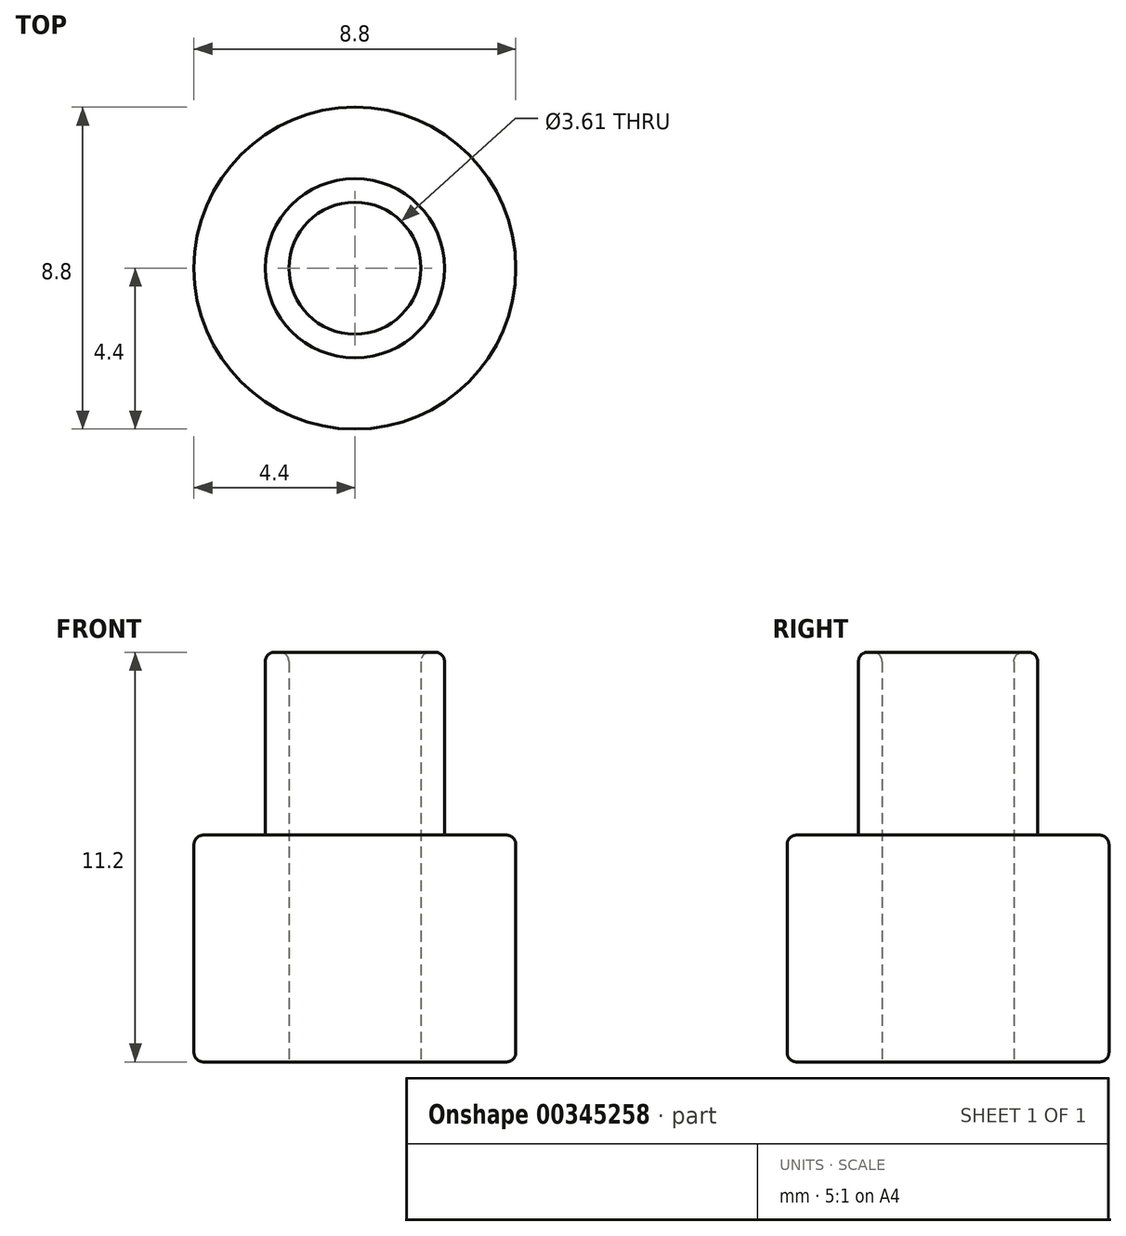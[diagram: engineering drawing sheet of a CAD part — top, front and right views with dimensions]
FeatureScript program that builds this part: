
annotation { "Feature Type Name" : "Feature", "Feature Type Description" : "" }
export const myFeature = defineFeature(function(context is Context, id is Id, definition is map)
    precondition{}
    {
        {
            var Q0;
            Q0=qCreatedBy(makeId("Top.planeOp"),FACE);
            var sketch = newSketch(context, id + "F0", { "sketchPlane" : qUnion([Q0])});
            skCircle(sketch, "E0", {"center": v(0, 0) * mm, "radius": 4.4 * mm});
            skSolve(sketch);
        }
        {
            var Q0;
            Q0 = qSketchRegion(id + "F0", true);
            extrude(context, id + "F1", {"entities" : qUnion([Q0]), "depth" : 6.2 * mm});
        }
        {
            var Q0;
            Q0=makeQuery(id+"F1.opExtrude","CAP_FACE",FACE,{"disambiguationData":[OSD([sQuery(id+"F0.wireOp",EDGE,"E0")])],"isStart":false});
            var sketch = newSketch(context, id + "F2", { "sketchPlane" : qUnion([Q0])});
            skCircle(sketch, "E1", {"center": v(0, 0) * mm, "radius": 2.45 * mm});
            skSolve(sketch);
        }
        {
            var Q0;
            Q0 = qSketchRegion(id + "F2", true);
            extrude(context, id + "F3", {"entities" : qUnion([Q0]), "operationType" : NewBodyOperationType.ADD, "depth" : 5 * mm});
        }
        {
            var Q0;
            Q0=makeQuery(id+"F1.opExtrude","CAP_FACE",FACE,{"disambiguationData":[OSD([sQuery(id+"F0.wireOp",EDGE,"E0")])],"isStart":true});
            var sketch = newSketch(context, id + "F4", { "sketchPlane" : qUnion([Q0])});
            skCircle(sketch, "E2", {"center": v(0, 0) * mm, "radius": 1.8 * mm});
            skSolve(sketch);
        }
        {
            var Q0;
            Q0 = qSketchRegion(id + "F4", true);
            extrude(context, id + "F5", {"entities" : qUnion([Q0]), "operationType" : NewBodyOperationType.REMOVE, "endBound" : BoundingType.THROUGH_ALL, "oppositeDirection" : true, "depth" : 25.4 * mm});
        }
        {
            var Q0;
            Q0=makeQuery(id+"F3.opExtrude","CAP_EDGE",EDGE,{"disambiguationData":[OSD([sQuery(id+"F2.wireOp",EDGE,"E1")])],"isStart":false});
            var Q1;
            Q1=makeQuery(id+"F5.boolean.opBoolean","INTERSECT",EDGE,{"derivedFrom":[makeQuery(id+"F3.opExtrude","CAP_FACE",FACE,{"disambiguationData":[OSD([sQuery(id+"F2.wireOp",EDGE,"E1")])],"isStart":false}),makeQuery(id+"F5.opExtrude","SWEPT_FACE",FACE,{"disambiguationData":[OSD([sQuery(id+"F4.wireOp",EDGE,"E2")])]})]});
            var Q2;
            Q2=makeQuery(id+"F1.opExtrude","CAP_EDGE",EDGE,{"disambiguationData":[OSD([sQuery(id+"F0.wireOp",EDGE,"E0")])],"isStart":true});
            var Q3;
            Q3=makeQuery(id+"F5.boolean.opBoolean","COPY",EDGE,{"derivedFrom":makeQuery(id+"F5.opExtrude","CAP_EDGE",EDGE,{"disambiguationData":[OSD([sQuery(id+"F4.wireOp",EDGE,"E2")])],"isStart":true})});
            var Q4;
            Q4=makeQuery(id+"F1.opExtrude","CAP_EDGE",EDGE,{"disambiguationData":[OSD([sQuery(id+"F0.wireOp",EDGE,"E0")])],"isStart":false});
            fillet(context, id + "F6", {"entities" : qUnion([Q0, Q1, Q2, Q3, Q4]), "radius" : 0.25 * mm, "tangentPropagation" : true, "allowEdgeOverflow" : false});
        }
    });
